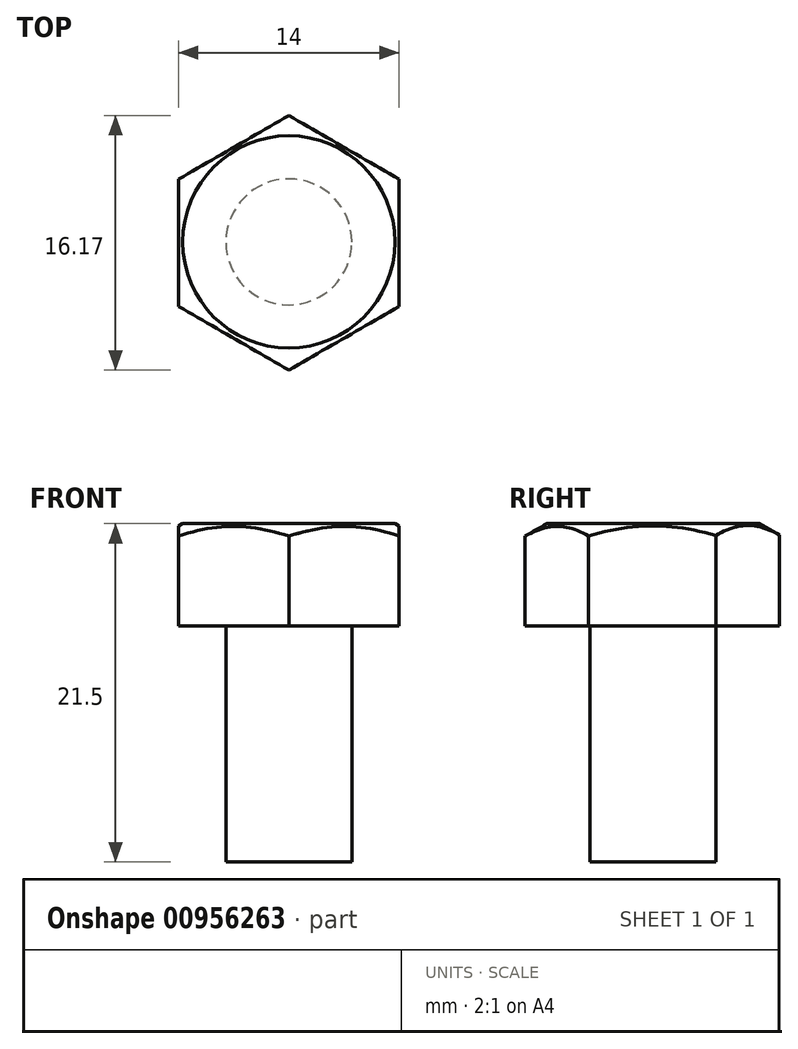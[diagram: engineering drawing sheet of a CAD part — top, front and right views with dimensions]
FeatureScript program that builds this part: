
annotation { "Feature Type Name" : "Feature", "Feature Type Description" : "" }
export const myFeature = defineFeature(function(context is Context, id is Id, definition is map)
    precondition{}
    {
        {
            var Q0;
            Q0=qCreatedBy(makeId("Top.planeOp"),FACE);
            var sketch = newSketch(context, id + "F0", { "sketchPlane" : qUnion([Q0])});
            skCircle(sketch, "E0", {"center": v(0, 0) * mm, "radius": 4 * mm});
            skSolve(sketch);
        }
        {
            var Q0;
            Q0 = qSketchRegion(id + "F0", true);
            extrude(context, id + "F1", {"entities" : qUnion([Q0]), "oppositeDirection" : true, "depth" : 15 * mm, "offsetDistance" : 25 * mm});
        }
        {
            var Q0;
            Q0=makeQuery(id+"F1.opExtrude","CAP_FACE",FACE,{"disambiguationData":[OSD([sQuery(id+"F0.wireOp",EDGE,"E0")])],"isStart":true});
            var sketch = newSketch(context, id + "F2", { "sketchPlane" : qUnion([Q0])});
            skLineSegment(sketch, "E1", {"start": v(0, 8.03) * mm, "end": v(-7, 3.98) * mm});
            skLineSegment(sketch, "E2", {"start": v(-7, 3.98) * mm, "end": v(-7, -4.1) * mm});
            skLineSegment(sketch, "E3", {"start": v(-7, -4.1) * mm, "end": v(0, -8.14) * mm});
            skLineSegment(sketch, "E4", {"start": v(0, -8.14) * mm, "end": v(7, -4.1) * mm});
            skLineSegment(sketch, "E5", {"start": v(7, -4.1) * mm, "end": v(7, 3.98) * mm});
            skLineSegment(sketch, "E6", {"start": v(7, 3.98) * mm, "end": v(0, 8.03) * mm});
            skSolve(sketch);
        }
        {
            var Q0;
            Q0 = qSketchRegion(id + "F2", true);
            extrude(context, id + "F3", {"entities" : qUnion([Q0]), "operationType" : NewBodyOperationType.ADD, "depth" : 6.5 * mm, "offsetDistance" : 25 * mm});
        }
        {
            var Q0;
            Q0=qCreatedBy(makeId("Right.planeOp"),FACE);
            var sketch = newSketch(context, id + "F4", { "sketchPlane" : qUnion([Q0])});
            skLineSegment(sketch, "E7", {"start": v(-6.74, 6.5) * mm, "end": v(-8.14, 6.5) * mm});
            skLineSegment(sketch, "E8", {"start": v(-8.14, 6.5) * mm, "end": v(-8.14, 5.7) * mm});
            skLineSegment(sketch, "E9", {"start": v(-8.14, 5.7) * mm, "end": v(-6.74, 6.5) * mm});
            skSolve(sketch);
        }
        {
            var Q0;
            Q0=makeQuery(id+"F3.opExtrude","CAP_FACE",FACE,{"disambiguationData":[OSD([sQuery(id+"F2.wireOp",EDGE,"E1"),sQuery(id+"F2.wireOp",EDGE,"E2"),sQuery(id+"F2.wireOp",EDGE,"E3"),sQuery(id+"F2.wireOp",EDGE,"E4"),sQuery(id+"F2.wireOp",EDGE,"E5"),sQuery(id+"F2.wireOp",EDGE,"E6")])],"isStart":false});
            var sketch = newSketch(context, id + "F5", { "sketchPlane" : qUnion([Q0])});
            skCircle(sketch, "E10", {"center": v(0, 0) * mm, "radius": 8.14 * mm});
            skSolve(sketch);
        }
        {
            var Q0;
            Q0 = qSketchRegion(id + "F4", true);
            var Q1;
            Q1=sQuery(id+"F5.wireOp",EDGE,"E10");
            sweep(context, id + "F6", {"operationType" : NewBodyOperationType.REMOVE, "profiles" : qUnion([Q0]), "path" : qUnion([Q1])});
        }
    });
